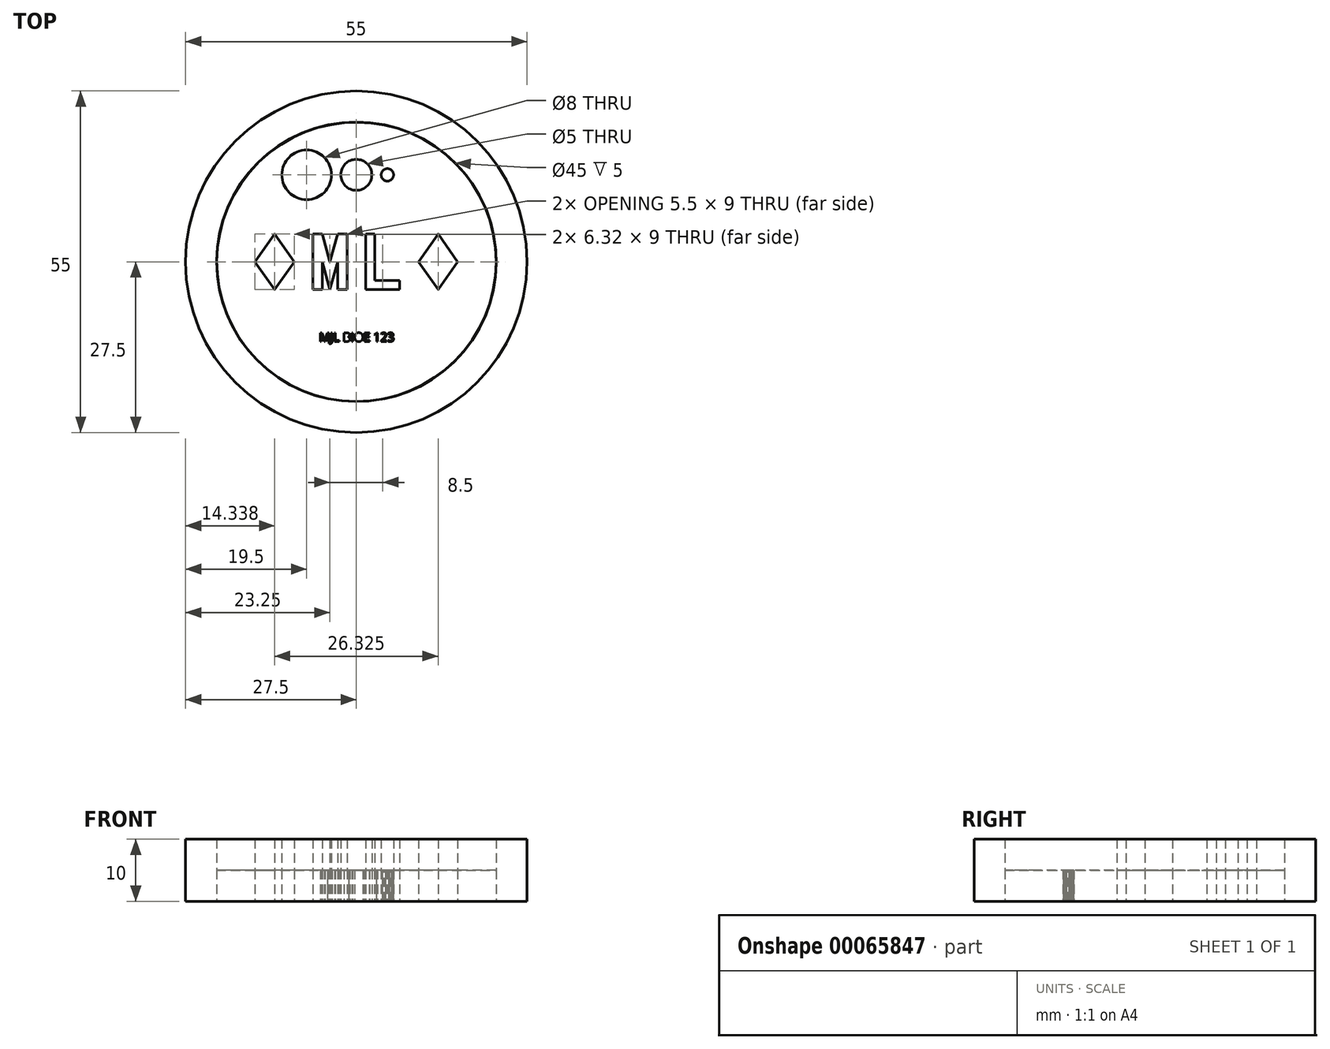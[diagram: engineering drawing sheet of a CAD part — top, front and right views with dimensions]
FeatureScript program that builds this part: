
annotation { "Feature Type Name" : "Feature", "Feature Type Description" : "" }
export const myFeature = defineFeature(function(context is Context, id is Id, definition is map)
    precondition{}
    {
        {
            var Q0;
            Q0=qCreatedBy(makeId("Top.planeOp"),FACE);
            var sketch = newSketch(context, id + "F0", { "sketchPlane" : qUnion([Q0])});
            skCircle(sketch, "E0", {"center": v(0, 0) * mm, "radius": 22.5 * mm});
            skCircle(sketch, "E1", {"center": v(0, 0) * mm, "radius": 27.5 * mm});
            skCircle(sketch, "E2", {"center": v(0, 14) * mm, "radius": 2.5 * mm});
            skCircle(sketch, "E3", {"center": v(-8, 14) * mm, "radius": 4 * mm});
            skCircle(sketch, "E4", {"center": v(5, 14) * mm, "radius": 1 * mm});
            skLineSegment(sketch, "E5", {"start": v(-7, 4.5) * mm, "end": v(-7, -4.5) * mm});
            skLineSegment(sketch, "E6", {"start": v(-7, -4.5) * mm, "end": v(-5.5, -4.5) * mm});
            skLineSegment(sketch, "E7", {"start": v(-5.5, -4.5) * mm, "end": v(-5.5, 0) * mm});
            skLineSegment(sketch, "E8", {"start": v(-5.5, 0) * mm, "end": v(-4.25, -4.5) * mm});
            skLineSegment(sketch, "E9", {"start": v(-4.25, -4.5) * mm, "end": v(-3, 0) * mm});
            skLineSegment(sketch, "E10", {"start": v(-3, 0) * mm, "end": v(-3, -4.5) * mm});
            skLineSegment(sketch, "E11", {"start": v(-3, -4.5) * mm, "end": v(-1.5, -4.5) * mm});
            skLineSegment(sketch, "E12", {"start": v(-1.5, -4.5) * mm, "end": v(-1.5, 4.5) * mm});
            skLineSegment(sketch, "E13", {"start": v(-1.5, 4.5) * mm, "end": v(-3, 4.5) * mm});
            skLineSegment(sketch, "E14", {"start": v(-3, 4.5) * mm, "end": v(-4.25, 0) * mm});
            skLineSegment(sketch, "E15", {"start": v(-4.25, 0) * mm, "end": v(-5.5, 4.5) * mm});
            skLineSegment(sketch, "E16", {"start": v(-5.5, 4.5) * mm, "end": v(-7, 4.5) * mm});
            skLineSegment(sketch, "E17", {"start": v(1.5, 4.5) * mm, "end": v(1.5, -4.5) * mm});
            skLineSegment(sketch, "E18", {"start": v(1.5, -4.5) * mm, "end": v(7, -4.5) * mm});
            skLineSegment(sketch, "E19", {"start": v(7, -4.5) * mm, "end": v(7, -3) * mm});
            skLineSegment(sketch, "E20", {"start": v(7, -3) * mm, "end": v(3, -3) * mm});
            skLineSegment(sketch, "E21", {"start": v(3, -3) * mm, "end": v(3, 4.5) * mm});
            skLineSegment(sketch, "E22", {"start": v(3, 4.5) * mm, "end": v(1.5, 4.5) * mm});
            skLineSegment(sketch, "E23", {"start": v(13.16, 4.5) * mm, "end": v(10, 0) * mm});
            skLineSegment(sketch, "E24", {"start": v(10, 0) * mm, "end": v(13.16, -4.5) * mm});
            skLineSegment(sketch, "E25", {"start": v(13.16, -4.5) * mm, "end": v(16.32, 0) * mm});
            skLineSegment(sketch, "E26", {"start": v(16.32, 0) * mm, "end": v(13.16, 4.5) * mm});
            skLineSegment(sketch, "E27", {"start": v(-10, 0) * mm, "end": v(-13.16, 4.5) * mm});
            skLineSegment(sketch, "E28", {"start": v(-13.16, -4.5) * mm, "end": v(-10, 0) * mm});
            skLineSegment(sketch, "E29", {"start": v(-16.32, 0) * mm, "end": v(-13.16, -4.5) * mm});
            skLineSegment(sketch, "E30", {"start": v(-13.16, 4.5) * mm, "end": v(-16.32, 0) * mm});
            skSolve(sketch);
        }
        {
            var Q0;
            Q0=makeQuery(id+"F0.imprint","IMPRINT",FACE,{"disambiguationData":[TD([[makeQuery(id+"F0.imprint","IMPRINT",EDGE,{"derivedFrom":sQuery(id+"F0.wireOp",EDGE,"E0")}),1.0]])]});
            extrude(context, id + "F1", {"entities" : qUnion([Q0]), "depth" : 5 * mm});
        }
        {
            var Q0;
            Q0=makeQuery(id+"F0.imprint","IMPRINT",FACE,{"disambiguationData":[TD([[makeQuery(id+"F0.imprint","IMPRINT",EDGE,{"derivedFrom":sQuery(id+"F0.wireOp",EDGE,"E0")}),-1.0]])]});
            var Q1;
            Q1=makeQuery(id+"F0.imprint","IMPRINT",FACE,{"disambiguationData":[TD([[makeQuery(id+"F0.imprint","IMPRINT",EDGE,{"derivedFrom":sQuery(id+"F0.wireOp",EDGE,"E3")}),1.0]])]});
            var Q2;
            Q2=makeQuery(id+"F0.imprint","IMPRINT",FACE,{"disambiguationData":[TD([[makeQuery(id+"F0.imprint","IMPRINT",EDGE,{"derivedFrom":sQuery(id+"F0.wireOp",EDGE,"E2")}),1.0]])]});
            var Q3;
            Q3=makeQuery(id+"F0.imprint","IMPRINT",FACE,{"disambiguationData":[TD([[makeQuery(id+"F0.imprint","IMPRINT",EDGE,{"derivedFrom":sQuery(id+"F0.wireOp",EDGE,"E4")}),1.0]])]});
            var Q4;
            Q4=makeQuery(id+"F0.imprint","IMPRINT",FACE,{"disambiguationData":[TD([[makeQuery(id+"F0.imprint","IMPRINT",EDGE,{"derivedFrom":sQuery(id+"F0.wireOp",EDGE,"E5")}),1.0]])]});
            var Q5;
            Q5=makeQuery(id+"F0.imprint","IMPRINT",FACE,{"disambiguationData":[TD([[makeQuery(id+"F0.imprint","IMPRINT",EDGE,{"derivedFrom":sQuery(id+"F0.wireOp",EDGE,"E17")}),1.0]])]});
            var Q6;
            Q6=makeQuery(id+"F0.imprint","IMPRINT",FACE,{"disambiguationData":[TD([[makeQuery(id+"F0.imprint","IMPRINT",EDGE,{"derivedFrom":sQuery(id+"F0.wireOp",EDGE,"E23")}),1.0]])]});
            var Q7;
            Q7=makeQuery(id+"F0.imprint","IMPRINT",FACE,{"disambiguationData":[TD([[makeQuery(id+"F0.imprint","IMPRINT",EDGE,{"derivedFrom":sQuery(id+"F0.wireOp",EDGE,"E27")}),1.0]])]});
            extrude(context, id + "F2", {"entities" : qUnion([Q0, Q1, Q2, Q3, Q4, Q5, Q6, Q7]), "operationType" : NewBodyOperationType.ADD, "depth" : 10 * mm});
        }
        {
            var Q0;
            Q0=qCreatedBy(makeId("Top.planeOp"),FACE);
            var sketch = newSketch(context, id + "F3", { "sketchPlane" : qUnion([Q0])});
            skCircle(sketch, "E31", {"center": v(0, 0) * mm, "radius": 22.5 * mm});
            skCircle(sketch, "E32", {"center": v(0, 14) * mm, "radius": 2.5 * mm});
            skCircle(sketch, "E33", {"center": v(-8, 14) * mm, "radius": 4 * mm});
            skCircle(sketch, "E34", {"center": v(5, 14) * mm, "radius": 1 * mm});
            skLineSegment(sketch, "E35", {"start": v(-7, 4.5) * mm, "end": v(-7, -4.5) * mm});
            skLineSegment(sketch, "E36", {"start": v(-7, -4.5) * mm, "end": v(-5.5, -4.5) * mm});
            skLineSegment(sketch, "E37", {"start": v(-5.5, -4.5) * mm, "end": v(-5.5, 0) * mm});
            skLineSegment(sketch, "E38", {"start": v(-5.5, 0) * mm, "end": v(-4.25, -4.5) * mm});
            skLineSegment(sketch, "E39", {"start": v(-4.25, -4.5) * mm, "end": v(-3, 0) * mm});
            skLineSegment(sketch, "E40", {"start": v(-3, 0) * mm, "end": v(-3, -4.5) * mm});
            skLineSegment(sketch, "E41", {"start": v(-3, -4.5) * mm, "end": v(-1.5, -4.5) * mm});
            skLineSegment(sketch, "E42", {"start": v(-1.5, -4.5) * mm, "end": v(-1.5, 4.5) * mm});
            skLineSegment(sketch, "E43", {"start": v(-1.5, 4.5) * mm, "end": v(-3, 4.5) * mm});
            skLineSegment(sketch, "E44", {"start": v(-3, 4.5) * mm, "end": v(-4.25, 0) * mm});
            skLineSegment(sketch, "E45", {"start": v(-4.25, 0) * mm, "end": v(-5.5, 4.5) * mm});
            skLineSegment(sketch, "E46", {"start": v(-5.5, 4.5) * mm, "end": v(-7, 4.5) * mm});
            skLineSegment(sketch, "E47", {"start": v(1.5, 4.5) * mm, "end": v(1.5, -4.5) * mm});
            skLineSegment(sketch, "E48", {"start": v(1.5, -4.5) * mm, "end": v(7, -4.5) * mm});
            skLineSegment(sketch, "E49", {"start": v(7, -4.5) * mm, "end": v(7, -3) * mm});
            skLineSegment(sketch, "E50", {"start": v(7, -3) * mm, "end": v(3, -3) * mm});
            skLineSegment(sketch, "E51", {"start": v(3, -3) * mm, "end": v(3, 4.5) * mm});
            skLineSegment(sketch, "E52", {"start": v(3, 4.5) * mm, "end": v(1.5, 4.5) * mm});
            skText(sketch, "E53", { "text": "MJL BIOE 123", "fontName": "OpenSans-Regular.ttf"});
            skCircle(sketch, "E54", {"center": v(0.03, -0.03) * mm, "radius": 22.5 * mm});
            skLineSegment(sketch, "E55", {"start": v(13.16, 4.5) * mm, "end": v(10, 0) * mm});
            skLineSegment(sketch, "E56", {"start": v(10, 0) * mm, "end": v(13.16, -4.5) * mm});
            skLineSegment(sketch, "E57", {"start": v(13.16, -4.5) * mm, "end": v(16.32, 0) * mm});
            skLineSegment(sketch, "E58", {"start": v(16.32, 0) * mm, "end": v(13.16, 4.5) * mm});
            skLineSegment(sketch, "E59", {"start": v(-10, 0) * mm, "end": v(-13.16, 4.5) * mm});
            skLineSegment(sketch, "E60", {"start": v(-13.16, -4.5) * mm, "end": v(-10, 0) * mm});
            skLineSegment(sketch, "E61", {"start": v(-16.32, 0) * mm, "end": v(-13.16, -4.5) * mm});
            skLineSegment(sketch, "E62", {"start": v(-13.16, 4.5) * mm, "end": v(-16.32, 0) * mm});
            const initialGuessF3  = {"E53": [-0.006, -0.01284, 1, 0, 0.00141]};
            skSetInitialGuess(sketch, initialGuessF3);
            skSolve(sketch);
        }
        {
            var Q0;
            Q0 = qSketchRegion(id + "F3", true);
            extrude(context, id + "F4", {"entities" : qUnion([Q0]), "depth" : 5 * mm});
        }
    });
